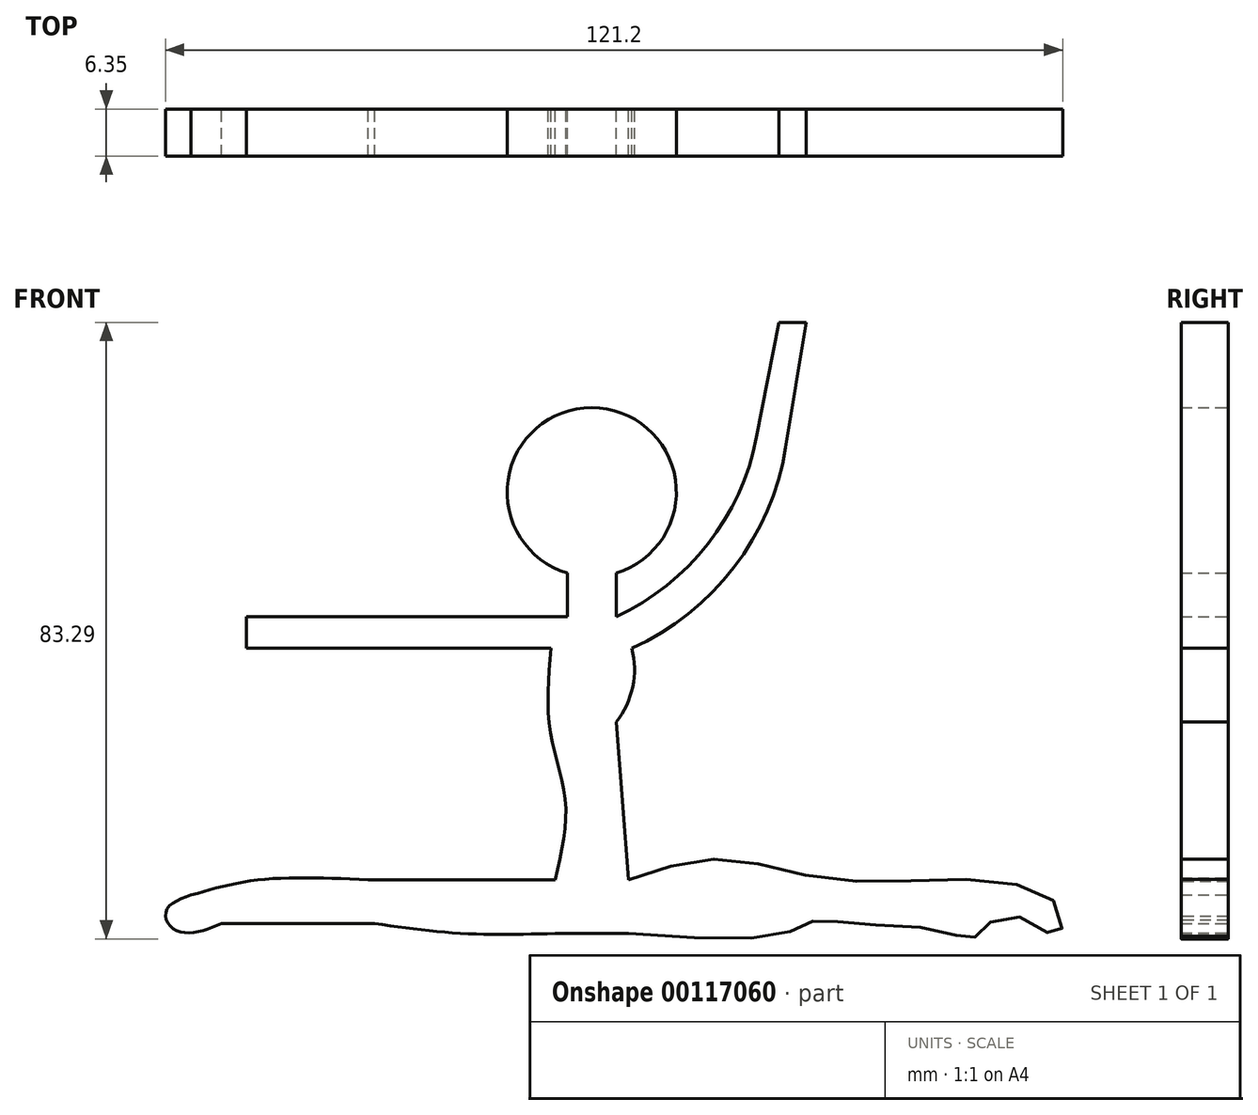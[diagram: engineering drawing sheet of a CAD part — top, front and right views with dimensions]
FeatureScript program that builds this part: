
annotation { "Feature Type Name" : "Feature", "Feature Type Description" : "" }
export const myFeature = defineFeature(function(context is Context, id is Id, definition is map)
    precondition{}
    {
        {
            var Q0;
            Q0=qCreatedBy(makeId("Front.planeOp"),FACE);
            var sketch = newSketch(context, id + "F0", { "sketchPlane" : qUnion([Q0])});
            skCircle(sketch, "E0", {"center": v(0, 21.1) * mm, "radius": 11.43 * mm});
            skLineSegment(sketch, "E1", {"start": v(-3.3, 10.16) * mm, "end": v(-3.3, 4.28) * mm});
            skLineSegment(sketch, "E2", {"start": v(3.3, 10.16) * mm, "end": v(3.3, 4.28) * mm});
            skArc(sketch, "E3", {"start": v(3.3, -9.94) * mm, "mid": v(5.79, -2.83) * mm, "end": v(3.3, 4.28) * mm});
            skLineSegment(sketch, "E4.bottom", {"start": v(2.39, -73.98) * mm, "end": v(2.39, -73.98) * mm});
            skFitSpline(sketch, "E5", {"points": [v(4.95, -31.28) * mm, v(17.58, -28.47) * mm, v(32.67, -31.28) * mm, v(52.45, -31.28) * mm, v(63.18, -35.18) * mm, v(62.85, -38.87) * mm, v(58.49, -36.52) * mm, v(53.12, -37.53) * mm, v(51.45, -39.2) * mm, v(47.42, -38.2) * mm, v(35.35, -37.2) * mm, v(29.98, -36.86) * mm, v(25.96, -38.53) * mm, v(4.95, -38.53) * mm], "startDerivative": vector(131.34, 46.33) * mm, "endDerivative": vector(-209.73, 14.17) * mm});
            skLineSegment(sketch, "E6", {"start": v(-4.95, -38.53) * mm, "end": v(4.95, -38.53) * mm});
            skLineSegment(sketch, "E7", {"start": v(3.3, -9.94) * mm, "end": v(4.95, -31.28) * mm});
            skFitSpline(sketch, "E8", {"points": [v(-5.54, 0) * mm, v(-5.59, -11.37) * mm, v(-3.54, -20.8) * mm, v(-4.95, -31.28) * mm], "startDerivative": vector(-2.68, -33.84) * mm, "endDerivative": vector(-7.52, -32.08) * mm});
            skArc(sketch, "E9", {"start": v(3.3, 4.28) * mm, "mid": v(15.7, 14.11) * mm, "end": v(22.27, 28.5) * mm});
            skFitSpline(sketch, "E10", {"points": [v(22.27, 28.5) * mm, v(25.29, 44.03) * mm], "startDerivative": vector(3.01, 15.52) * mm, "endDerivative": vector(3.01, 15.52) * mm});
            skLineSegment(sketch, "E11", {"start": v(25.29, 44.03) * mm, "end": v(29, 44.03) * mm});
            skLineSegment(sketch, "E12", {"start": v(29, 44.03) * mm, "end": v(26.21, 27.12) * mm});
            skArc(sketch, "E13", {"start": v(5.43, 0) * mm, "mid": v(19.22, 10.96) * mm, "end": v(26.21, 27.12) * mm});
            skLineSegment(sketch, "E14", {"start": v(-3.3, 4.28) * mm, "end": v(-46.63, 4.28) * mm});
            skLineSegment(sketch, "E15", {"start": v(-46.63, 4.28) * mm, "end": v(-46.63, 0) * mm});
            skLineSegment(sketch, "E16", {"start": v(-46.63, 0) * mm, "end": v(-5.54, 0) * mm});
            skLineSegment(sketch, "E17", {"start": v(-4.95, -31.28) * mm, "end": v(-30.2, -31.28) * mm});
            skFitSpline(sketch, "E18", {"points": [v(-30.2, -31.28) * mm, v(-44.94, -31.28) * mm, v(-54.12, -33.34) * mm], "startDerivative": vector(-28.13, 1.29) * mm, "endDerivative": vector(-19.37, -5.67) * mm});
            skFitSpline(sketch, "E19", {"points": [v(-54.12, -33.34) * mm, v(-57.4, -35.27) * mm, v(-56.99, -37.52) * mm, v(-54.12, -38.43) * mm, v(-50, -37.19) * mm], "startDerivative": vector(-15.8, -5.74) * mm, "endDerivative": vector(14.59, 6.13) * mm});
            skLineSegment(sketch, "E20", {"start": v(-50, -37.19) * mm, "end": v(-29.33, -37.19) * mm});
            skFitSpline(sketch, "E21", {"points": [v(-29.33, -37.19) * mm, v(-17.26, -38.53) * mm, v(-4.95, -38.53) * mm], "startDerivative": vector(24.14, -3.38) * mm, "endDerivative": vector(24.62, 0.68) * mm});
            skSolve(sketch);
        }
        {
            var Q0;
            Q0 = qSketchRegion(id + "FYtpbaQTXLORzBN_0", true);
            var Q1;
            Q1 = qSketchRegion(id + "F0", true);
            var Q2;
            {var subQ0=sQuery(id+"F0.wireOp",EDGE,"E0");var subQ1=makeQuery(id+"F0.imprint","INTERSECT",VERTEX,{"derivedFrom":[subQ0,sQuery(id+"F0.wireOp",EDGE,"E1")]});Q2=makeQuery(id+"F0.imprint","IMPRINT",FACE,{"disambiguationData":[TD([[makeQuery(id+"F0.imprint","IMPRINT",EDGE,{"disambiguationData":[TD([[subQ1,-1.0]])],"derivedFrom":subQ0}),1.0]])]});}
            extrude(context, id + "F1", {"entities" : qUnion([Q0, Q1, Q2]), "depth" : 6.35 * mm});
        }
    });
